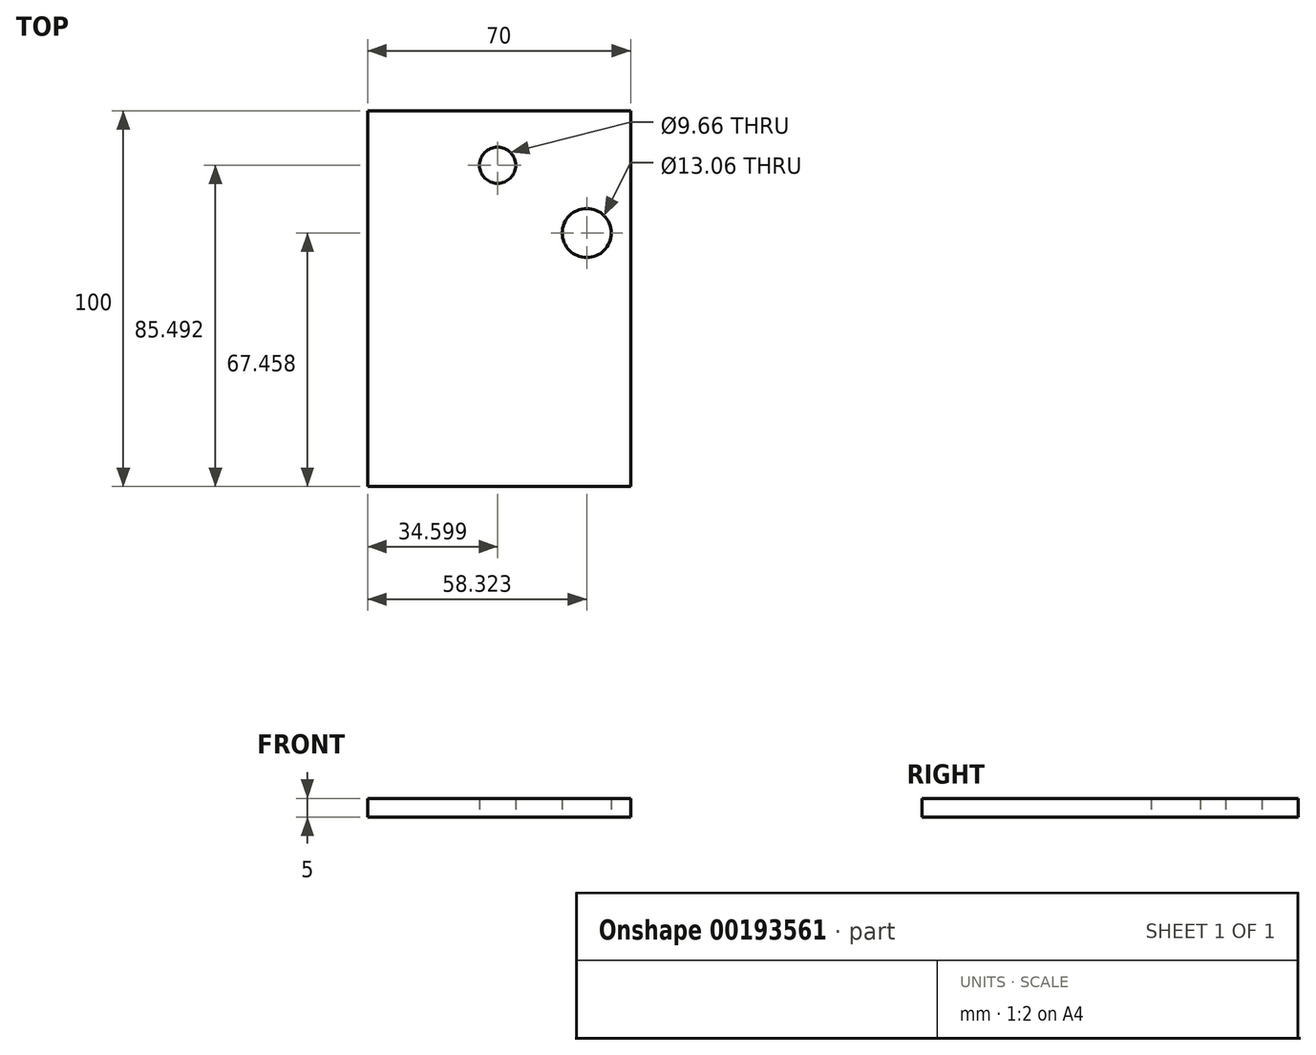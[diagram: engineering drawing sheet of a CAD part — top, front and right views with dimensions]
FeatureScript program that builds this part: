
annotation { "Feature Type Name" : "Feature", "Feature Type Description" : "" }
export const myFeature = defineFeature(function(context is Context, id is Id, definition is map)
    precondition{}
    {
        {
            var Q0;
            Q0=qCreatedBy(makeId("Top.planeOp"),FACE);
            var sketch = newSketch(context, id + "F0", { "sketchPlane" : qUnion([Q0])});
            skLineSegment(sketch, "E0.bottom", {"start": v(35, 50) * mm, "end": v(-35, 50) * mm});
            skLineSegment(sketch, "E0.top", {"start": v(35, -50) * mm, "end": v(-35, -50) * mm});
            skLineSegment(sketch, "E0.left", {"start": v(35, 50) * mm, "end": v(35, -50) * mm});
            skLineSegment(sketch, "E0.right", {"start": v(-35, 50) * mm, "end": v(-35, -50) * mm});
            skPoint(sketch, "E0.middle", {"position": v(0, 0) * mm});
            skCircle(sketch, "E1", {"center": v(-0.4, 35.5) * mm, "radius": 4.83 * mm});
            skPoint(sketch, "E1.first.point", {"position": v(0, 30.68) * mm});
            skPoint(sketch, "E1.second.point", {"position": v(2.8, 39.1) * mm});
            skPoint(sketch, "E1.third.point", {"position": v(0, 40.3) * mm});
            skCircle(sketch, "E2", {"center": v(23.32, 17.46) * mm, "radius": 6.53 * mm});
            skPoint(sketch, "E2.first.point", {"position": v(16.84, 18.25) * mm});
            skPoint(sketch, "E2.second.point", {"position": v(22.06, 23.86) * mm});
            skPoint(sketch, "E2.third.point", {"position": v(17.65, 14.24) * mm});
            skSolve(sketch);
        }
        {
            var Q0;
            Q0=makeQuery(id+"F0.imprint","IMPRINT",FACE,{"disambiguationData":[TD([[makeQuery(id+"F0.imprint","IMPRINT",EDGE,{"derivedFrom":sQuery(id+"F0.wireOp",EDGE,"E0.bottom")}),1.0]])]});
            extrude(context, id + "F1", {"entities" : qUnion([Q0]), "depth" : 5 * mm});
        }
    });
